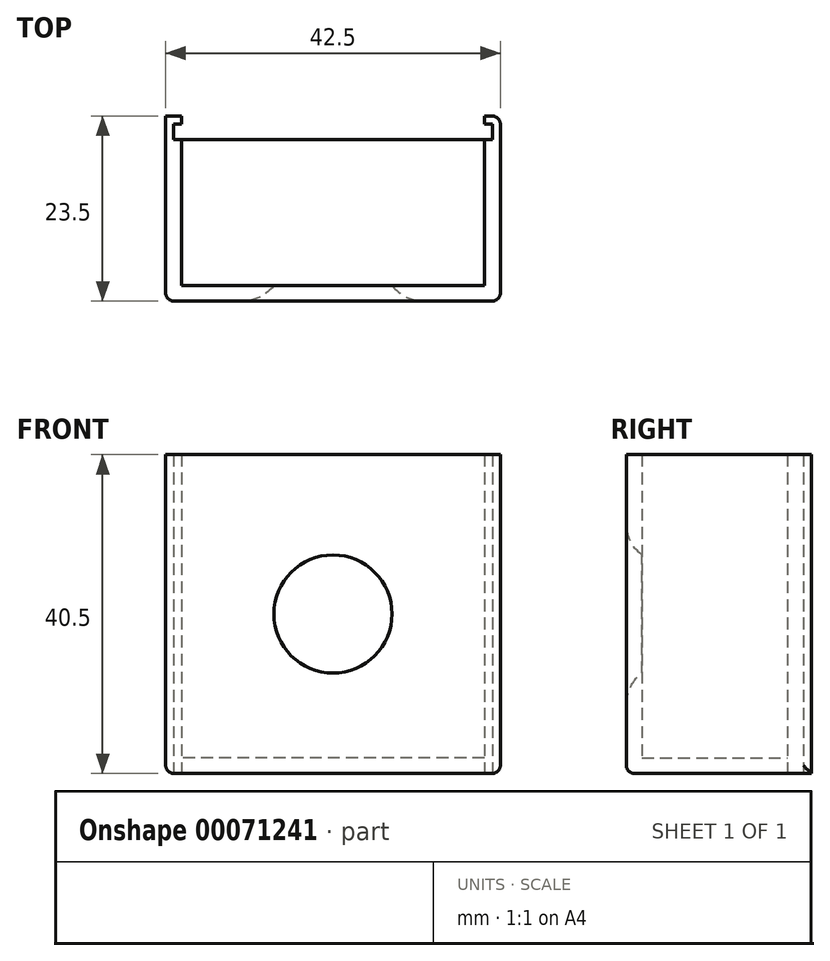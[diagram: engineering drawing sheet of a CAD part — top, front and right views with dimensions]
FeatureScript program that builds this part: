
annotation { "Feature Type Name" : "Feature", "Feature Type Description" : "" }
export const myFeature = defineFeature(function(context is Context, id is Id, definition is map)
    precondition{}
    {
        {
            var Q0;
            Q0=qCreatedBy(makeId("Top.planeOp"),FACE);
            var sketch = newSketch(context, id + "F0", { "sketchPlane" : qUnion([Q0])});
            skLineSegment(sketch, "E0.rect.bottom", {"start": v(21.25, -10.25) * mm, "end": v(-21.25, -10.25) * mm});
            skLineSegment(sketch, "E0.rect.top", {"start": v(21.25, 10.25) * mm, "end": v(-21.25, 10.25) * mm});
            skLineSegment(sketch, "E0.rect.left", {"start": v(21.25, -10.25) * mm, "end": v(21.25, 10.25) * mm});
            skLineSegment(sketch, "E0.rect.right", {"start": v(-21.25, -10.25) * mm, "end": v(-21.25, 10.25) * mm});
            skPoint(sketch, "E0.rect.middle", {"position": v(0, 0) * mm});
            skSolve(sketch);
        }
        {
            var Q0;
            Q0=sQuery(id+"F0.wireOp",EDGE,"E0.rect.bottom");
            cPlane(context, id + "F1", {"entities" : qUnion([Q0]), "cplaneType" : CPlaneType.LINE_ANGLE, "offset" : 0 * mm, "angle" : 0 * degree, "width" : 152.4 * mm, "height" : 152.4 * mm});
        }
        {
            var Q0;
            Q0=qCreatedBy(id+"F1.planeOp",FACE);
            var sketch = newSketch(context, id + "F2", { "sketchPlane" : qUnion([Q0])});
            skLineSegment(sketch, "E1.rect.bottom", {"start": v(-21.25, 0) * mm, "end": v(21.25, 0) * mm});
            skLineSegment(sketch, "E1.rect.top", {"start": v(-21.25, 40.5) * mm, "end": v(21.25, 40.5) * mm});
            skLineSegment(sketch, "E1.rect.left", {"start": v(-21.25, 0) * mm, "end": v(-21.25, 40.5) * mm});
            skLineSegment(sketch, "E1.rect.right", {"start": v(21.25, 0) * mm, "end": v(21.25, 40.5) * mm});
            skPoint(sketch, "E1.rect.middle", {"position": v(0, 20.25) * mm});
            skCircle(sketch, "E2", {"center": v(0, 20.25) * mm, "radius": 7.5 * mm});
            skSolve(sketch);
        }
        {
            var Q0;
            Q0=sQuery(id+"F0.wireOp",EDGE,"E0.rect.left");
            cPlane(context, id + "F3", {"entities" : qUnion([Q0]), "cplaneType" : CPlaneType.LINE_ANGLE, "offset" : 0 * mm, "angle" : 90 * degree, "width" : 152.4 * mm, "height" : 152.4 * mm});
        }
        {
            var Q0;
            Q0=sQuery(id+"F0.wireOp",EDGE,"E0.rect.right");
            cPlane(context, id + "F4", {"entities" : qUnion([Q0]), "cplaneType" : CPlaneType.LINE_ANGLE, "offset" : 0 * mm, "angle" : 270 * degree, "width" : 152.4 * mm, "height" : 152.4 * mm});
        }
        {
            var Q0;
            Q0=qCreatedBy(id+"F3.planeOp",FACE);
            var sketch = newSketch(context, id + "F5", { "sketchPlane" : qUnion([Q0])});
            skLineSegment(sketch, "E3.rect.bottom", {"start": v(-10.25, 0) * mm, "end": v(13.25, 0) * mm});
            skLineSegment(sketch, "E3.rect.top", {"start": v(-10.25, 40.5) * mm, "end": v(13.25, 40.5) * mm});
            skLineSegment(sketch, "E3.rect.left", {"start": v(-10.25, 0) * mm, "end": v(-10.25, 40.5) * mm});
            skLineSegment(sketch, "E3.rect.right", {"start": v(13.25, 0) * mm, "end": v(13.25, 40.5) * mm});
            skPoint(sketch, "E3.rect.middle", {"position": v(1.5, 20.25) * mm});
            skSolve(sketch);
        }
        {
            var Q0;
            Q0=qCreatedBy(id+"F4.planeOp",FACE);
            var sketch = newSketch(context, id + "F6", { "sketchPlane" : qUnion([Q0])});
            skLineSegment(sketch, "E4.rect.bottom", {"start": v(-13.25, 0) * mm, "end": v(10.25, 0) * mm});
            skLineSegment(sketch, "E4.rect.top", {"start": v(-13.25, 40.5) * mm, "end": v(10.25, 40.5) * mm});
            skLineSegment(sketch, "E4.rect.left", {"start": v(-13.25, 0) * mm, "end": v(-13.25, 40.5) * mm});
            skLineSegment(sketch, "E4.rect.right", {"start": v(10.25, 0) * mm, "end": v(10.25, 40.5) * mm});
            skPoint(sketch, "E4.rect.middle", {"position": v(-1.5, 20.25) * mm});
            skSolve(sketch);
        }
        {
            var Q0;
            Q0=qCreatedBy(makeId("Top.planeOp"),FACE);
            var sketch = newSketch(context, id + "F7", { "sketchPlane" : qUnion([Q0])});
            skLineSegment(sketch, "E5.rect.bottom", {"start": v(20.25, 12.25) * mm, "end": v(19.25, 12.25) * mm});
            skLineSegment(sketch, "E5.rect.top", {"start": v(20.25, 10.25) * mm, "end": v(19.25, 10.25) * mm});
            skLineSegment(sketch, "E5.rect.left", {"start": v(20.25, 12.25) * mm, "end": v(20.25, 10.25) * mm});
            skLineSegment(sketch, "E5.rect.right", {"start": v(19.25, 12.25) * mm, "end": v(19.25, 10.25) * mm});
            skPoint(sketch, "E5.rect.middle", {"position": v(19.75, 11.25) * mm});
            skLineSegment(sketch, "E6.MirrorCS", {"start": v(-19.25, 12.25) * mm, "end": v(-19.25, 10.25) * mm});
            skLineSegment(sketch, "E7.MirrorCS", {"start": v(-20.25, 10.25) * mm, "end": v(-19.25, 10.25) * mm});
            skLineSegment(sketch, "E8.MirrorCS", {"start": v(-20.25, 12.25) * mm, "end": v(-20.25, 10.25) * mm});
            skLineSegment(sketch, "E9.MirrorCS", {"start": v(-20.25, 12.25) * mm, "end": v(-19.25, 12.25) * mm});
            skSolve(sketch);
        }
        {
            var Q0;
            Q0=makeQuery(id+"F2.imprint","IMPRINT",FACE,{"disambiguationData":[TD([[makeQuery(id+"F2.imprint","IMPRINT",EDGE,{"derivedFrom":sQuery(id+"F2.wireOp",EDGE,"E1.rect.bottom")}),1.0]])]});
            extrude(context, id + "F8", {"entities" : qUnion([Q0]), "oppositeDirection" : true, "depth" : 2 * mm});
        }
        {
            var Q0;
            Q0=makeQuery(id+"F6.imprint","IMPRINT",FACE,{"disambiguationData":[TD([[makeQuery(id+"F6.imprint","IMPRINT",EDGE,{"derivedFrom":sQuery(id+"F6.wireOp",EDGE,"E4.rect.bottom")}),1.0]])]});
            extrude(context, id + "F9", {"entities" : qUnion([Q0]), "operationType" : NewBodyOperationType.ADD, "oppositeDirection" : true, "depth" : 2 * mm});
        }
        {
            var Q0;
            Q0=makeQuery(id+"F5.imprint","IMPRINT",FACE,{"disambiguationData":[TD([[makeQuery(id+"F5.imprint","IMPRINT",EDGE,{"derivedFrom":sQuery(id+"F5.wireOp",EDGE,"E3.rect.bottom")}),1.0]])]});
            extrude(context, id + "F10", {"entities" : qUnion([Q0]), "operationType" : NewBodyOperationType.ADD, "oppositeDirection" : true, "depth" : 2 * mm});
        }
        {
            var Q0;
            Q0=makeQuery(id+"F0.imprint","IMPRINT",FACE,{"disambiguationData":[TD([[makeQuery(id+"F0.imprint","IMPRINT",EDGE,{"derivedFrom":sQuery(id+"F0.wireOp",EDGE,"E0.rect.bottom")}),-1.0]])]});
            extrude(context, id + "F11", {"entities" : qUnion([Q0]), "operationType" : NewBodyOperationType.ADD, "depth" : 2 * mm});
        }
        {
            var Q0;
            Q0=makeQuery(id+"F7.imprint","IMPRINT",FACE,{"disambiguationData":[TD([[makeQuery(id+"F7.imprint","IMPRINT",EDGE,{"derivedFrom":sQuery(id+"F7.wireOp",EDGE,"E6.MirrorCS")}),-1.0]])]});
            var Q1;
            Q1=makeQuery(id+"F7.imprint","IMPRINT",FACE,{"disambiguationData":[TD([[makeQuery(id+"F7.imprint","IMPRINT",EDGE,{"derivedFrom":sQuery(id+"F7.wireOp",EDGE,"E5.rect.bottom")}),1.0]])]});
            extrude(context, id + "F12", {"entities" : qUnion([Q0, Q1]), "operationType" : NewBodyOperationType.REMOVE, "oppositeDirection" : true, "depth" : 38.5 * mm});
        }
        {
            var Q0;
            Q0 = qSketchRegion(id + "F7", true);
            extrude(context, id + "F13", {"entities" : qUnion([Q0]), "operationType" : NewBodyOperationType.REMOVE, "depth" : 40.5 * mm});
        }
        {
            var Q0;
            Q0=makeQuery(id+"F8.opExtrude","CAP_EDGE",EDGE,{"disambiguationData":[OSD([sQuery(id+"F2.wireOp",EDGE,"E1.rect.bottom")])],"isStart":true});
            var Q1;
            Q1=makeQuery(id+"F10.boolean.opBoolean","MERGE",EDGE,{"derivedFrom":[makeQuery(id+"F8.opExtrude","SWEPT_EDGE",EDGE,{"disambiguationData":[OSD([sQuery(id+"F2.wireOp",EDGE,"E1.rect.bottom"),sQuery(id+"F2.wireOp",EDGE,"E1.rect.right")])]}),makeQuery(id+"F10.opExtrude","CAP_EDGE",EDGE,{"disambiguationData":[OSD([sQuery(id+"F5.wireOp",EDGE,"E3.rect.bottom")])],"isStart":true})]});
            var Q2;
            Q2=makeQuery(id+"F10.opExtrude","CAP_EDGE",EDGE,{"disambiguationData":[OSD([sQuery(id+"F5.wireOp",EDGE,"E3.rect.right")])],"isStart":true});
            var Q3;
            Q3=makeQuery(id+"F8.opExtrude","CAP_EDGE",EDGE,{"disambiguationData":[OSD([sQuery(id+"F2.wireOp",EDGE,"E1.rect.right")])],"isStart":true});
            var Q4;
            Q4=makeQuery(id+"F8.opExtrude","CAP_EDGE",EDGE,{"disambiguationData":[OSD([sQuery(id+"F2.wireOp",EDGE,"E1.rect.left")])],"isStart":true});
            var Q5;
            Q5=makeQuery(id+"F9.boolean.opBoolean","MERGE",EDGE,{"derivedFrom":[makeQuery(id+"F8.opExtrude","SWEPT_EDGE",EDGE,{"disambiguationData":[OSD([sQuery(id+"F2.wireOp",EDGE,"E1.rect.bottom"),sQuery(id+"F2.wireOp",EDGE,"E1.rect.left")])]}),makeQuery(id+"F9.opExtrude","CAP_EDGE",EDGE,{"disambiguationData":[OSD([sQuery(id+"F6.wireOp",EDGE,"E4.rect.bottom")])],"isStart":true})]});
            fillet(context, id + "F14", {"entities" : qUnion([Q0, Q1, Q2, Q3, Q4, Q5]), "radius" : 1 * mm, "tangentPropagation" : true, "allowEdgeOverflow" : false});
        }
        {
            var Q0;
            Q0=makeQuery(id+"F8.opExtrude","CAP_EDGE",EDGE,{"disambiguationData":[OSD([sQuery(id+"F2.wireOp",EDGE,"E2")])],"isStart":true});
            fillet(context, id + "F15", {"entities" : qUnion([Q0]), "radius" : 5.08 * mm, "tangentPropagation" : true, "allowEdgeOverflow" : false});
        }
    });
